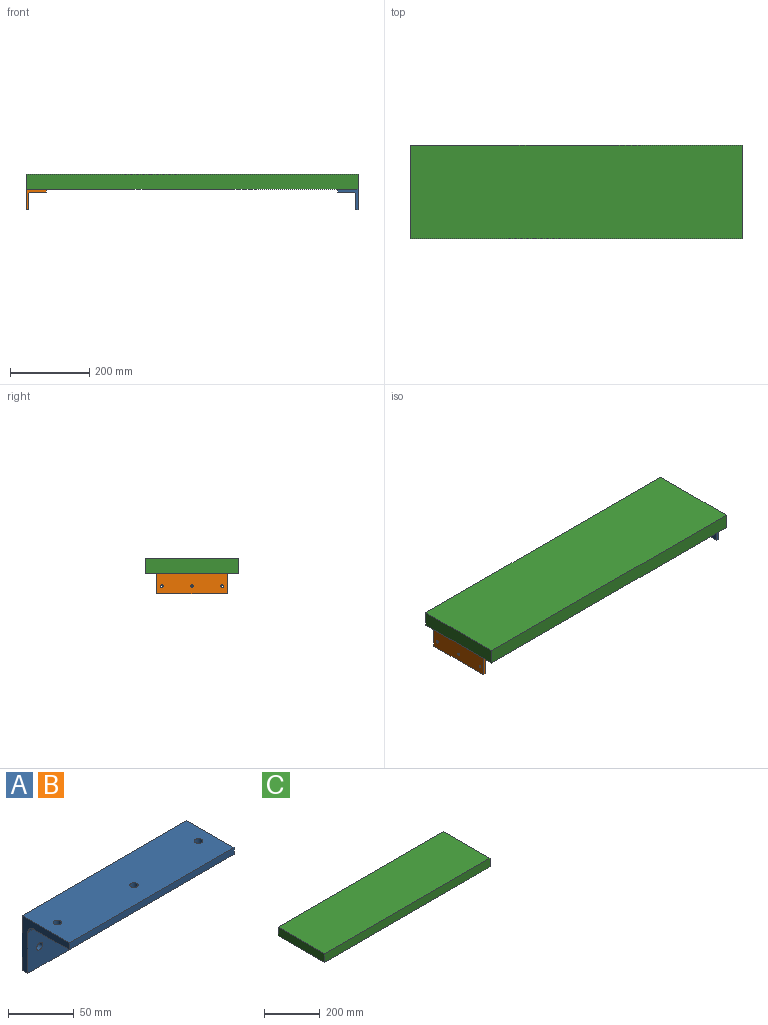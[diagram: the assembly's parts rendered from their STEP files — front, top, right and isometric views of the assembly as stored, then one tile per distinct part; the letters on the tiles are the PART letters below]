
ASSEMBLY  parts=3 mates=6
PART A: 15 faces, bbox 177.8x50.8x50.8 mm
  f0: plane 177.8x38.1mm, normal (0,0,-1), area 6679.2mm2, adj f4,f6,f7,f8,f12,f13,f14
  f1: plane 177.8x50.8mm, normal (0,0,1), area 8937.2mm2, adj f3,f4,f6,f7,f12,f13,f14
  f2: plane 177.8x38.1mm, normal (0,-1,0), area 6679.2mm2, adj f5,f6,f7,f8,f9,f10,f11
  f3: plane 177.8x50.8mm, normal (0,1,0), area 8937.2mm2, adj f1,f5,f6,f7,f9,f10,f11
  f4: plane 177.8x6.35mm, normal (0,-1,0), area 1129mm2, adj f0,f1,f6,f7
  f5: plane 177.8x6.35mm, normal (0,0,-1), area 1129mm2, adj f2,f3,f6,f7
  f6: plane 50.8x50.8mm, normal (1,0,0), area 613.5mm2, adj f0,f1,f2,f3,f4,f5,f8
  f7: plane 50.8x50.8mm, normal (-1,0,0), area 613.5mm2, adj f0,f1,f2,f3,f4,f5,f8
  f8: cylinder r=6.35mm len=177.8mm, axis (1,0,0), area 1773.5mm2, adj f0,f2,f6,f7
  f9: cylinder r=3.17mm len=6.35mm, axis (0,-1,0), area 126.7mm2, adj f2,f3
  f10: cylinder r=3.17mm len=6.35mm, axis (0,-1,0), area 126.7mm2, adj f2,f3
  f11: cylinder r=3.17mm len=6.35mm, axis (0,-1,0), area 126.7mm2, adj f2,f3
  f12: cylinder r=3.17mm len=6.35mm, axis (0,0,1), area 126.7mm2, adj f0,f1
  f13: cylinder r=3.17mm len=6.35mm, axis (0,0,1), area 126.7mm2, adj f0,f1
  f14: cylinder r=3.17mm len=6.35mm, axis (0,0,1), area 126.7mm2, adj f0,f1
PART B: same geometry as A
PART C: 6 faces, bbox 838.2x235x38.1 mm
  f0: plane 838.2x234.95mm, normal (0,0,1), area 196935.1mm2, adj f1,f3,f4,f5
  f1: plane 838.2x38.1mm, normal (0,-1,0), area 31935.4mm2, adj f0,f2,f4,f5
  f2: plane 838.2x234.95mm, normal (0,0,-1), area 196935.1mm2, adj f1,f3,f4,f5
  f3: plane 838.2x38.1mm, normal (0,1,0), area 31935.4mm2, adj f0,f2,f4,f5
  f4: plane 234.95x38.1mm, normal (-1,0,0), area 8951.6mm2, adj f0,f1,f2,f3
  f5: plane 234.95x38.1mm, normal (1,0,0), area 8951.6mm2, adj f0,f1,f2,f3
PLACE A rot(axis=(0,0,-1),90deg) t=(419.1,0,-19.05)mm
PLACE B rot(axis=(0,0,1),90deg) t=(-419.1,0,-19.05)mm
PLACE C at identity fixed
MATE planar B.f3 <-> C.f4  axis (-1,0,0) through (-419.1,0,-44.38)mm
MATE planar A.f1 <-> C.f2  axis (0,0,1) through (393.72,0,-19.05)mm
MATE fastened B.f3 <-> C.f4  axis (-1,0,0) through (-419.1,0,-19.05)mm
MATE planar C.f5 <-> A.f3  axis (1,0,0) through (419.1,0,0)mm
MATE planar A.f6 <-> B.f7  axis (0,-1,0) through (419.1,-88.9,-19.05)mm
MATE planar B.f1 <-> C.f2  axis (0,0,1) through (-393.72,0,-19.05)mm
